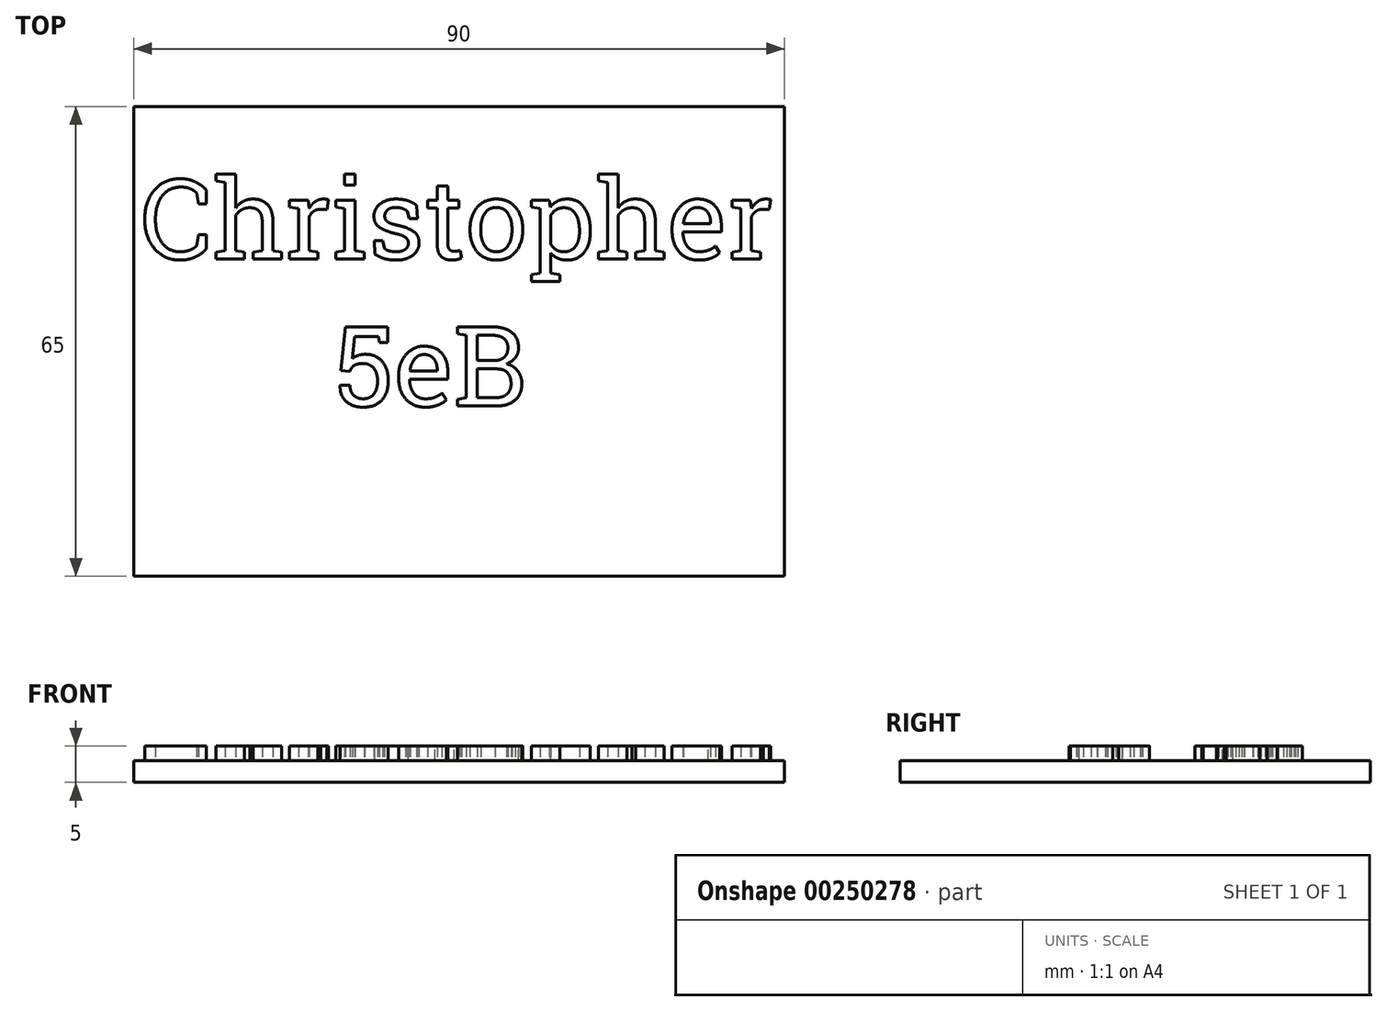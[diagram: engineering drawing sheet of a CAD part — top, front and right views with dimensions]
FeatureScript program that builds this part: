
annotation { "Feature Type Name" : "Feature", "Feature Type Description" : "" }
export const myFeature = defineFeature(function(context is Context, id is Id, definition is map)
    precondition{}
    {
        {
            var Q0;
            Q0=qCreatedBy(makeId("Top.planeOp"),FACE);
            var sketch = newSketch(context, id + "F0", { "sketchPlane" : qUnion([Q0])});
            skLineSegment(sketch, "E0.bottom", {"start": v(0, 0) * mm, "end": v(90, 0) * mm});
            skLineSegment(sketch, "E0.top", {"start": v(0, -65) * mm, "end": v(90, -65) * mm});
            skLineSegment(sketch, "E0.left", {"start": v(0, 0) * mm, "end": v(0, -65) * mm});
            skLineSegment(sketch, "E0.right", {"start": v(90, 0) * mm, "end": v(90, -65) * mm});
            skSolve(sketch);
        }
        {
            var Q0;
            Q0=makeQuery(id+"F0.imprint","IMPRINT",FACE,{"disambiguationData":[TD([[makeQuery(id+"F0.imprint","IMPRINT",EDGE,{"derivedFrom":sQuery(id+"F0.wireOp",EDGE,"E0.bottom")}),-1.0]])]});
            extrude(context, id + "F1", {"entities" : qUnion([Q0]), "depth" : 3 * mm});
        }
        {
            var Q0;
            Q0=makeQuery(id+"F1.opExtrude","CAP_FACE",FACE,{"disambiguationData":[OSD([sQuery(id+"F0.wireOp",EDGE,"E0.bottom"),sQuery(id+"F0.wireOp",EDGE,"E0.top"),sQuery(id+"F0.wireOp",EDGE,"E0.left"),sQuery(id+"F0.wireOp",EDGE,"E0.right")])],"isStart":false});
            var sketch = newSketch(context, id + "F2", { "sketchPlane" : qUnion([Q0])});
            skText(sketch, "E1", { "text": "Christopher \n       5eB", "fontName": "RobotoSlab-Regular.ttf"});
            const initialGuessF2  = {"E1": [0.001, -0.0211, 1, 0, 0.0111]};
            skSetInitialGuess(sketch, initialGuessF2);
            skSolve(sketch);
        }
        {
            var Q0;
            Q0 = qSketchRegion(id + "F2", true);
            extrude(context, id + "F3", {"entities" : qUnion([Q0]), "operationType" : NewBodyOperationType.ADD, "depth" : 2 * mm});
        }
    });
